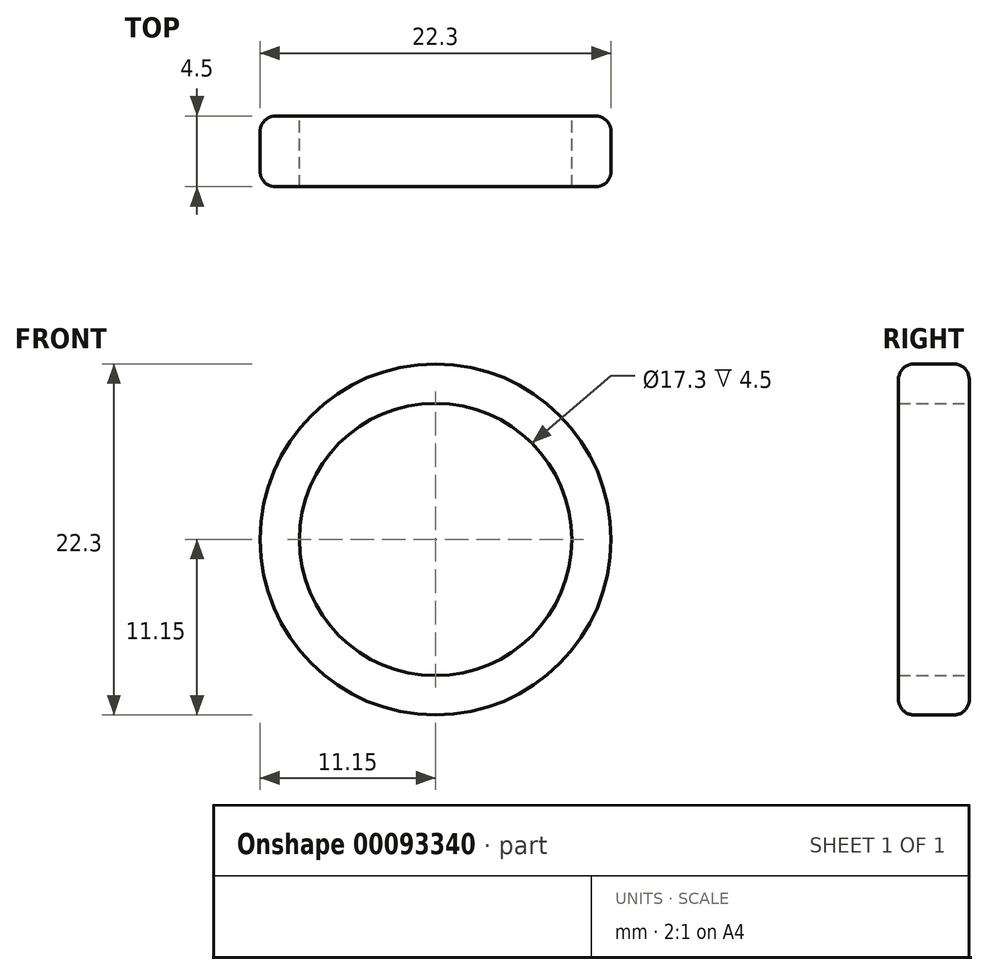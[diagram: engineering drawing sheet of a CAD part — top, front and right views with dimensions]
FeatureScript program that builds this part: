
annotation { "Feature Type Name" : "Feature", "Feature Type Description" : "" }
export const myFeature = defineFeature(function(context is Context, id is Id, definition is map)
    precondition{}
    {
        {
            var Q0;
            Q0=qCreatedBy(makeId("Front.planeOp"),FACE);
            var sketch = newSketch(context, id + "F0", { "sketchPlane" : qUnion([Q0])});
            skCircle(sketch, "E0", {"center": v(0, 0) * mm, "radius": 8.65 * mm});
            skCircle(sketch, "E1.0", {"center": v(0, 0) * mm, "radius": 11.15 * mm});
            skPoint(sketch, "E2", {"position": v(11.15, 0) * mm});
            skPoint(sketch, "E3", {"position": v(-11.15, 0) * mm});
            skLineSegment(sketch, "E4", {"start": v(11.15, 0) * mm, "end": v(11.15, 11.15) * mm});
            skLineSegment(sketch, "E5", {"start": v(11.15, 11.15) * mm, "end": v(0, 11.15) * mm});
            skLineSegment(sketch, "E6.MirrorCS", {"start": v(-11.15, 11.15) * mm, "end": v(0, 11.15) * mm});
            skLineSegment(sketch, "E7.MirrorCS", {"start": v(-11.15, 0) * mm, "end": v(-11.15, 11.15) * mm});
            skSolve(sketch);
        }
        {
            var Q0;
            Q0=makeQuery(id+"F0.imprint","IMPRINT",FACE,{"disambiguationData":[TD([[makeQuery(id+"F0.imprint","IMPRINT",EDGE,{"derivedFrom":sQuery(id+"F0.wireOp",EDGE,"E0")}),-1.0]])]});
            extrude(context, id + "F1", {"entities" : qUnion([Q0]), "depth" : 2.25 * mm, "hasSecondDirection" : true, "secondDirectionOppositeDirection" : true, "secondDirectionDepth" : 2.25 * mm});
        }
        {
            var Q0;
            Q0=makeQuery(id+"F1.opExtrude","CAP_EDGE",EDGE,{"disambiguationData":[OSD([sQuery(id+"F0.wireOp",EDGE,"E1.0")])],"isStart":false});
            var Q1;
            Q1=makeQuery(id+"F1.opExtrude","CAP_EDGE",EDGE,{"disambiguationData":[OSD([sQuery(id+"F0.wireOp",EDGE,"E1.0")])],"isStart":true});
            var Q2;
            Q2=makeQuery(id+"F1.opExtrude","CAP_EDGE",EDGE,{"disambiguationData":[OSD([sQuery(id+"F0.wireOp",EDGE,"E4")])],"isStart":false});
            var Q3;
            Q3=makeQuery(id+"F1.opExtrude","CAP_EDGE",EDGE,{"disambiguationData":[OSD([sQuery(id+"F0.wireOp",EDGE,"E4")])],"isStart":true});
            fillet(context, id + "F2", {"entities" : qUnion([Q0, Q1, Q2, Q3]), "radius" : 1 * mm, "tangentPropagation" : true, "allowEdgeOverflow" : false});
        }
    });
